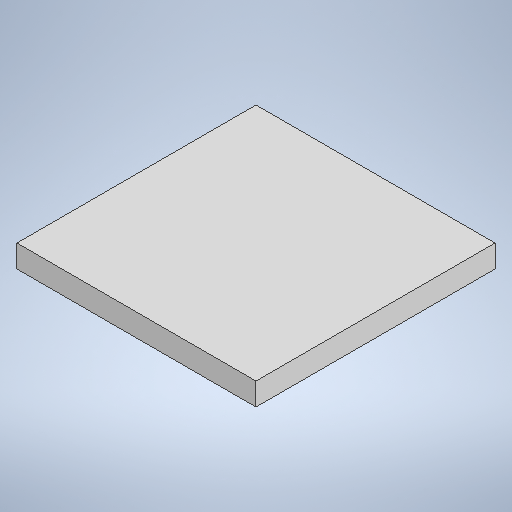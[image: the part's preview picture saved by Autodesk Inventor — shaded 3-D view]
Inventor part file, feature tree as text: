
AUTODESK INVENTOR PART (.ipt)
format: ipt  version: 2025 (Build 290162010, 162A)  size: 248,320 bytes
history: native  units: mm
features: other x2, sheet_metal_op x1, sketch x1
ambient origin geometry x8: Origin, YZ Plane, XZ Plane, XY Plane, X Axis, Y Axis, Z Axis, Center Point
bodies: Solid1 (feature_tree)
feature tree (4):
  sheet_metal_op  "Face1"
  sketch  "Sketch1"  dims[d0=85.0mm d4=85.0mm d10=8.0mm]
  other  "Plate1"
  other  "Definition1"
